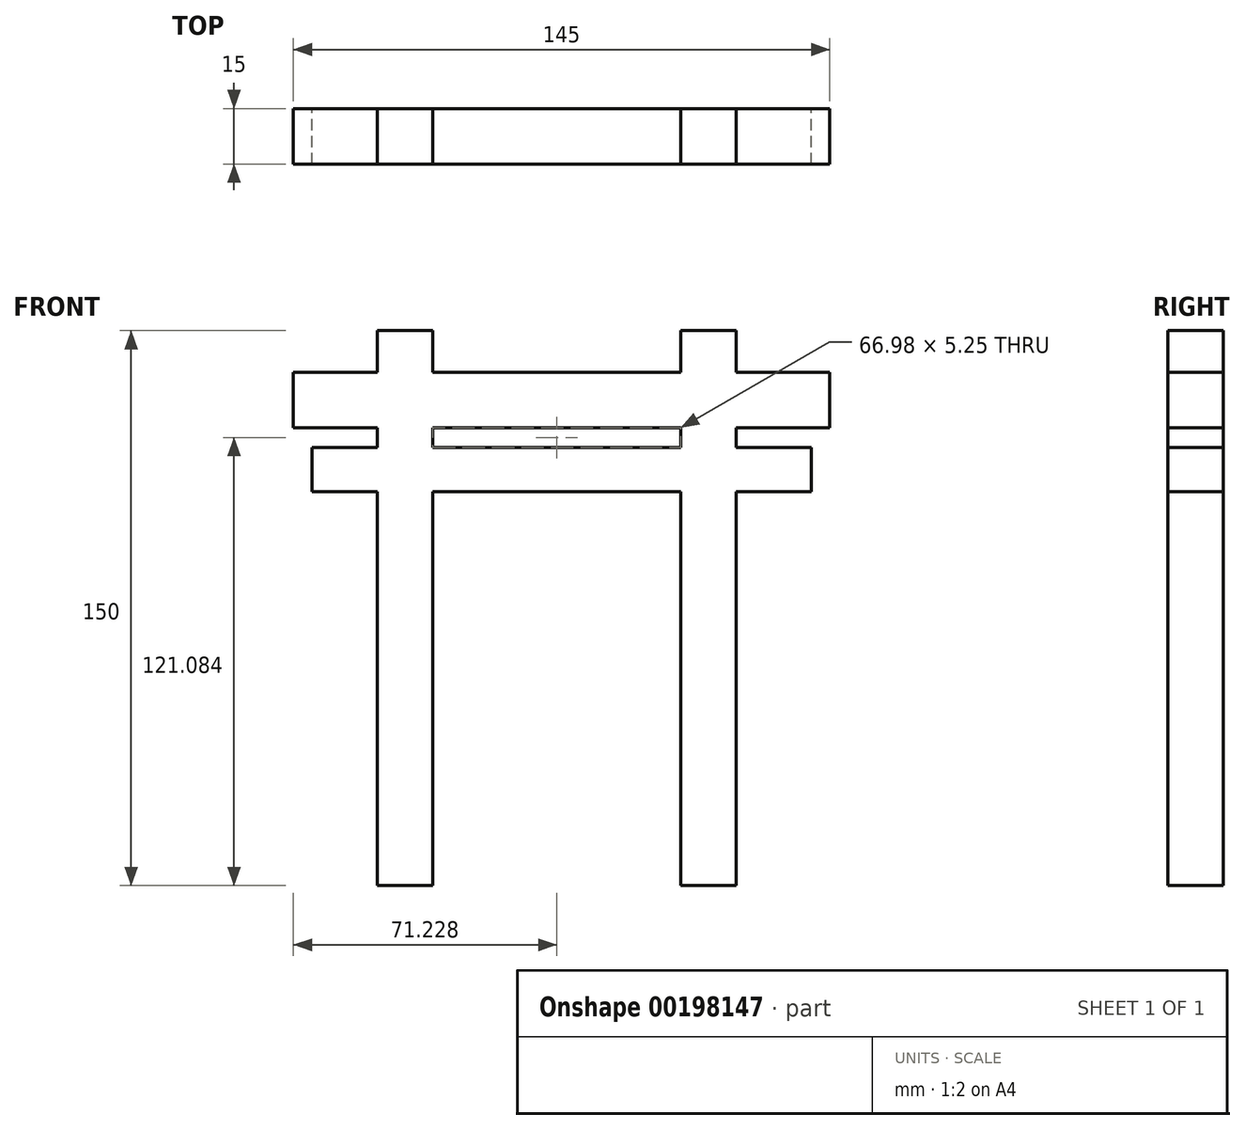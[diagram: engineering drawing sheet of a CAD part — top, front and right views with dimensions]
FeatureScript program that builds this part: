
annotation { "Feature Type Name" : "Feature", "Feature Type Description" : "" }
export const myFeature = defineFeature(function(context is Context, id is Id, definition is map)
    precondition{}
    {
        {
            var Q0;
            Q0=qCreatedBy(makeId("Top.planeOp"),FACE);
            var sketch = newSketch(context, id + "F0", { "sketchPlane" : qUnion([Q0])});
            skLineSegment(sketch, "E0.bottom", {"start": v(-49.76, 7.5) * mm, "end": v(-34.76, 7.5) * mm});
            skLineSegment(sketch, "E0.top", {"start": v(-49.76, -7.5) * mm, "end": v(-34.76, -7.5) * mm});
            skLineSegment(sketch, "E0.left", {"start": v(-49.76, 7.5) * mm, "end": v(-49.76, -7.5) * mm});
            skLineSegment(sketch, "E0.right", {"start": v(-34.76, 7.5) * mm, "end": v(-34.76, -7.5) * mm});
            skPoint(sketch, "E0.middle", {"position": v(-42.26, 0) * mm});
            skLineSegment(sketch, "E1.bottom", {"start": v(47.22, 7.5) * mm, "end": v(32.22, 7.5) * mm});
            skLineSegment(sketch, "E1.top", {"start": v(47.22, -7.5) * mm, "end": v(32.22, -7.5) * mm});
            skLineSegment(sketch, "E1.left", {"start": v(47.22, 7.5) * mm, "end": v(47.22, -7.5) * mm});
            skLineSegment(sketch, "E1.right", {"start": v(32.22, 7.5) * mm, "end": v(32.22, -7.5) * mm});
            skPoint(sketch, "E1.middle", {"position": v(39.72, 0) * mm});
            skSolve(sketch);
        }
        {
            var Q0;
            Q0=makeQuery(id+"F0.imprint","IMPRINT",FACE,{"disambiguationData":[TD([[makeQuery(id+"F0.imprint","IMPRINT",EDGE,{"derivedFrom":sQuery(id+"F0.wireOp",EDGE,"E0.bottom")}),-1.0]])]});
            var Q1;
            Q1=makeQuery(id+"F0.imprint","IMPRINT",FACE,{"disambiguationData":[TD([[makeQuery(id+"F0.imprint","IMPRINT",EDGE,{"derivedFrom":sQuery(id+"F0.wireOp",EDGE,"E1.bottom")}),1.0]])]});
            extrude(context, id + "F1", {"entities" : qUnion([Q0, Q1]), "depth" : 150 * mm});
        }
        {
            var Q0;
            Q0=makeQuery(id+"F1.opExtrude","SWEPT_BODY",BODY,{"disambiguationData":[OSD([sQuery(id+"F0.wireOp",EDGE,"E0.bottom"),sQuery(id+"F0.wireOp",EDGE,"E0.top"),sQuery(id+"F0.wireOp",EDGE,"E0.left"),sQuery(id+"F0.wireOp",EDGE,"E0.right")])]});
            var Q1;
            Q1=makeQuery(id+"F1.opExtrude","SWEPT_BODY",BODY,{"disambiguationData":[OSD([sQuery(id+"F0.wireOp",EDGE,"E1.bottom"),sQuery(id+"F0.wireOp",EDGE,"E1.top"),sQuery(id+"F0.wireOp",EDGE,"E1.left"),sQuery(id+"F0.wireOp",EDGE,"E1.right")])]});
            transform(context, id + "F2", {"entities" : qUnion([Q0, Q1]), "transformType" : TransformType.TRANSLATION_3D, "dx" : 0 * mm, "dy" : 0 * mm, "dz" : -75.4 * mm, "makeCopy" : false});
        }
        {
            var Q0;
            Q0=qCreatedBy(makeId("Front.planeOp"),FACE);
            var sketch = newSketch(context, id + "F3", { "sketchPlane" : qUnion([Q0])});
            skLineSegment(sketch, "E2.bottom", {"start": v(-67.5, 31.06) * mm, "end": v(67.5, 31.06) * mm});
            skLineSegment(sketch, "E2.top", {"start": v(-67.5, 43.06) * mm, "end": v(67.5, 43.06) * mm});
            skLineSegment(sketch, "E2.left", {"start": v(-67.5, 31.06) * mm, "end": v(-67.5, 43.06) * mm});
            skLineSegment(sketch, "E2.right", {"start": v(67.5, 31.06) * mm, "end": v(67.5, 43.06) * mm});
            skPoint(sketch, "E2.middle", {"position": v(0, 37.06) * mm});
            skSolve(sketch);
        }
        {
            var Q0;
            Q0=makeQuery(id+"F3.imprint","IMPRINT",FACE,{"disambiguationData":[TD([[makeQuery(id+"F3.imprint","IMPRINT",EDGE,{"derivedFrom":sQuery(id+"F3.wireOp",EDGE,"E2.bottom")}),1.0]])]});
            extrude(context, id + "F4", {"entities" : qUnion([Q0]), "operationType" : NewBodyOperationType.ADD, "endBound" : BoundingType.SYMMETRIC, "depth" : 15 * mm});
        }
        {
            var Q0;
            Q0=qCreatedBy(makeId("Front.planeOp"),FACE);
            var sketch = newSketch(context, id + "F5", { "sketchPlane" : qUnion([Q0])});
            skLineSegment(sketch, "E3.bottom", {"start": v(-72.5, 63.3) * mm, "end": v(72.5, 63.3) * mm});
            skLineSegment(sketch, "E3.top", {"start": v(-72.5, 48.3) * mm, "end": v(72.5, 48.3) * mm});
            skLineSegment(sketch, "E3.left", {"start": v(-72.5, 63.3) * mm, "end": v(-72.5, 48.3) * mm});
            skLineSegment(sketch, "E3.right", {"start": v(72.5, 63.3) * mm, "end": v(72.5, 48.3) * mm});
            skPoint(sketch, "E3.middle", {"position": v(0, 55.8) * mm});
            skSolve(sketch);
        }
        {
            var Q0;
            Q0 = qSketchRegion(id + "F5", true);
            extrude(context, id + "F6", {"entities" : qUnion([Q0]), "operationType" : NewBodyOperationType.ADD, "endBound" : BoundingType.SYMMETRIC, "depth" : 15 * mm});
        }
    });
